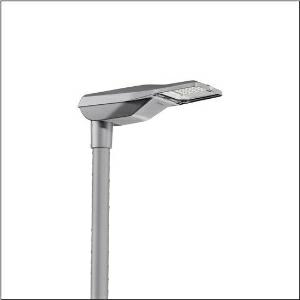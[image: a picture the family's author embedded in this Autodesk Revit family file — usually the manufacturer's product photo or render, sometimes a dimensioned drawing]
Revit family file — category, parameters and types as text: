
# Revit family: streetlight_sl_21_iq_micro___st1_5a_5xe1p41g08db_1f20
name_source: partatom
category: Lighting Fixtures
units: mm (PartAtom-declared; Revit-internal decimal feet)

## family parameters
Cut with Voids When Loaded = No
Host = Face
Light Source = No
Part Type = Normal
Room Calculation Point = No
Round Connector Dimension = Use Diameter
Shared = No

## types (1)
- --- (1 x LED, 4930 lm, 36.4 W, 4000K)
    Apparent Load = 36 VA
    CIE Flux Codes = 22 53 95 100 100
    Color Rendering = 70
    Color Temperature = 4000K
    Default Elevation = 1800 mm
    Description = Streetlight SL 21 iQ micro, mast luminaire, primary light control with lens, of PMMA, primary optical cover: cover, of toughened safety glass, transparent, light distribution: ST1.5a, light emission: direct distribution, primary light characteristic: asymmetric, installation type: post-top, side-entry, LED, High Power LED, rated luminous flux: 4.930lm, luminous efficacy: 135lm/W, light colour: 740, colour temperature: 4000K, control gear: iQ Street-Remote, control: Street-Remote, Auto-Match, Temp-Guard, Lumen-Switch, Night-Set, Smart-Wire, Light-Fading, Desk-Remote (wireless, voltage-free reading and setting of iQ features in the workshop via application-optimized NFC function/RFID function), optimised constant luminous flux control (CLO 2.0), pre-setting: linear dimming characteristic, mains connection: 220..240V, AC, 50/60Hz, start of lifetime: 36W, end of service life: 38W, reduction: 16W, luminaire housing, of diecast aluminium, powder-coated, SITECO metallic grey (DB 702S), corrosivity category C5 high according to DIN EN ISO 12944, please order mast flange separately, inclination adjustable: 0°, 5°, 10°, 15°, sealing non-destructively replaceable, multi-level sealing system, length: 528mm, width: 235mm, height: 110mm, mast flange for spigot size: 42mm (side-entry): 5XC10008XM4, 60/48mm (side-entry/post-top): 5XC10108XM2, 76/60mm (side-entry/post-top): 5XC10108XM1, protection rating (complete): IP66, insulation class (complete): insulation class II (safety insulation), certification: CE, ENEC, ENEC+, VDE, impact resistance: IK10, permissible operating ambient temperature for outdoor applications: -40..+50°C, standard-compliant lighting for roads and squares, packaging unit: 1 piece

Light Distribution: ST1.5a
    Height = 110 mm
    Lamp = 1 x LED
    Lamp Light Flux = 4930 lm
    Lamp Power = 36.4 W
    Lamp count = 1
    Length = 528 mm
    Luminous efficacy = 135 lm/W
    Manufacturer = Siteco
    ModVariant = No
    Model = 5XE1P41G08DB
    Number of Poles = 1
    OnlyDefault = Yes
    Power Factor = 1
    Product Name = Streetlight SL 21 iQ micro | ST1.5a
    Product group = mast luminaire | pylon top
    ProductGroupID = 6100
    Protection Class = Protection class II
    Protection Degree = IP 66
    RLX_Detail_Level = 1
    RLX_Emergency_Light_Flux = 0 lm
    RLX_Emergency_Type = 0
    RLX_Emergency_Type_DB = No
    RlxData = <blob elided: 103317 chars, md5=047b5cc1>
    Socket = socket
    Standby Power = 0 W
    System Light Flux = 4930 lm
    System Power = 36 W
    Type Comments = factory setting: luminous flux: 100 % | dim-lin: 254 | 715 mA
    Type Image = l_1006881.jpg
    URL = http://relux.com
    VarID = @adj_153279
    Voltage = 0 V
    Weight = 0.00 kg
    Width = 235 mm

## geometry (parser evidence)
native form markers: Blend x4, Sweep x11
no freeform markers — native parametric forms only
